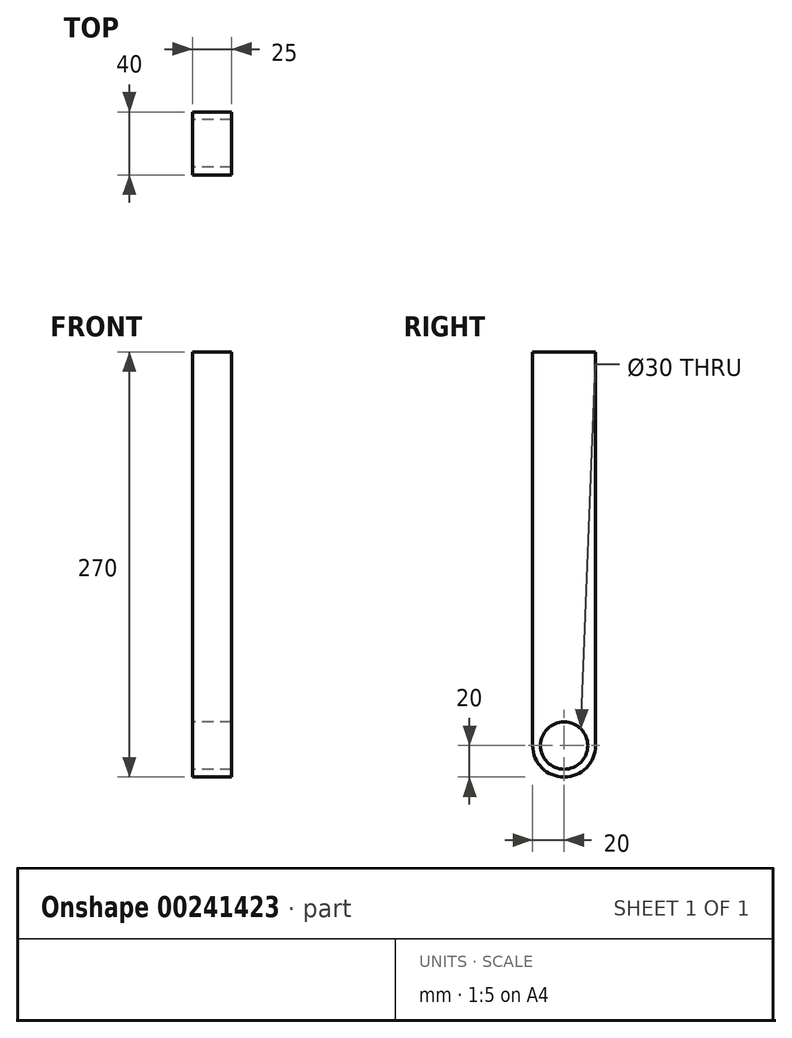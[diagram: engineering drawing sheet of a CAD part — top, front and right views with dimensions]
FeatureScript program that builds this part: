
annotation { "Feature Type Name" : "Feature", "Feature Type Description" : "" }
export const myFeature = defineFeature(function(context is Context, id is Id, definition is map)
    precondition{}
    {
        {
            var Q0;
            Q0=qCreatedBy(makeId("Right.planeOp"),FACE);
            var sketch = newSketch(context, id + "F0", { "sketchPlane" : qUnion([Q0])});
            skLineSegment(sketch, "E0.bottom", {"start": v(-20, 0) * mm, "end": v(20, 0) * mm});
            skLineSegment(sketch, "E0.top", {"start": v(-20, 250) * mm, "end": v(20, 250) * mm});
            skLineSegment(sketch, "E0.left", {"start": v(-20, 0) * mm, "end": v(-20, 250) * mm});
            skLineSegment(sketch, "E0.right", {"start": v(20, 0) * mm, "end": v(20, 250) * mm});
            skCircle(sketch, "E1", {"center": v(0, 0) * mm, "radius": 15 * mm});
            skCircle(sketch, "E2", {"center": v(0, 0) * mm, "radius": 20 * mm});
            skSolve(sketch);
        }
        {
            var Q0;
            Q0 = qSketchRegion(id + "F0", true);
            extrude(context, id + "F1", {"entities" : qUnion([Q0]), "depth" : 25 * mm});
        }
    });
